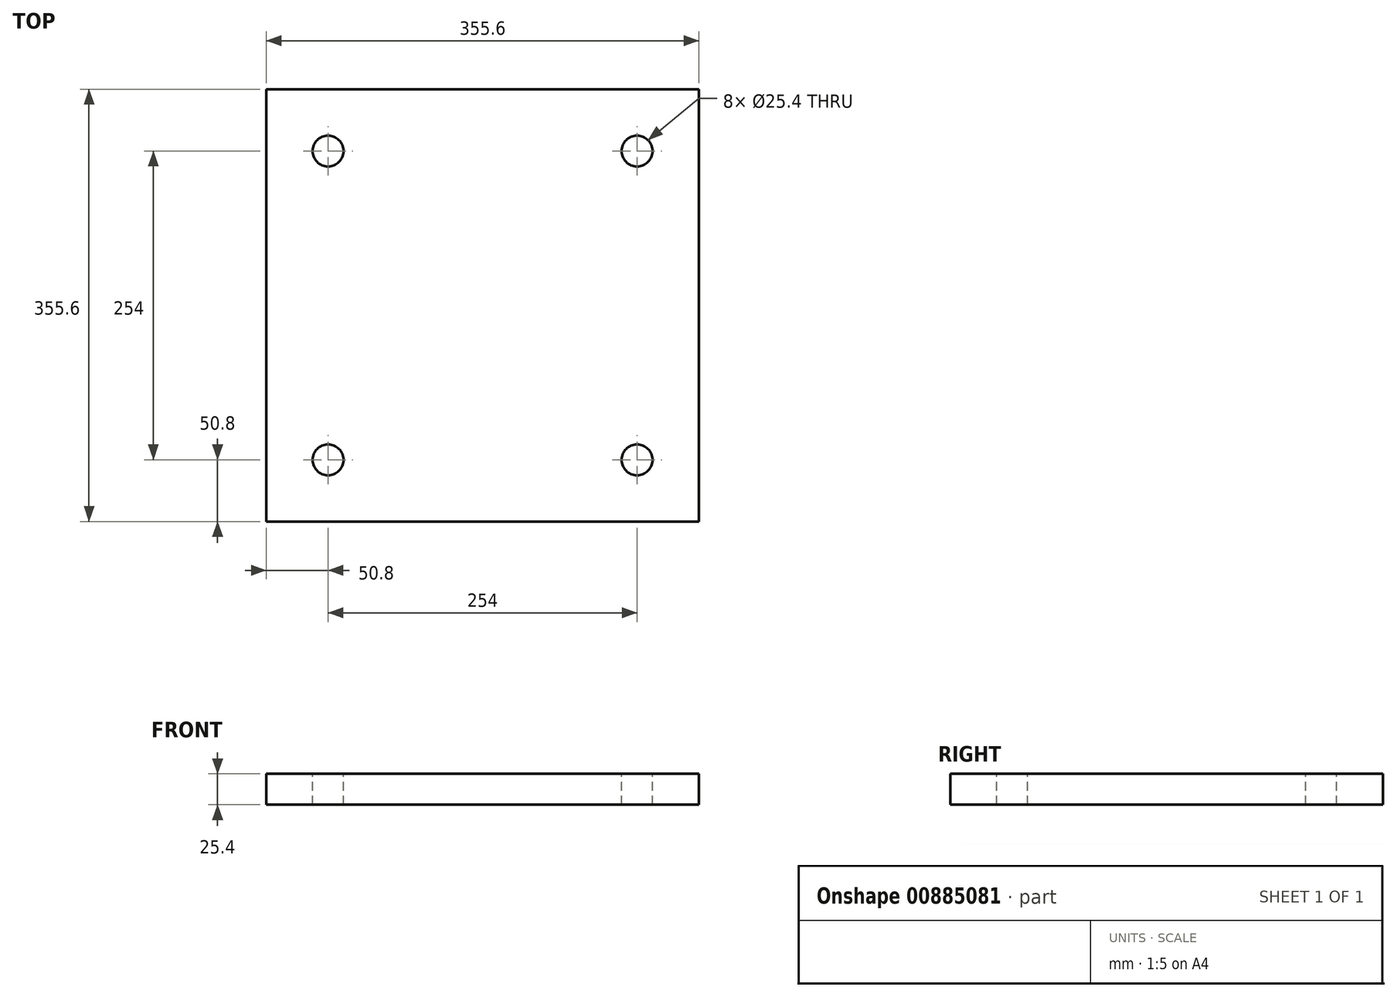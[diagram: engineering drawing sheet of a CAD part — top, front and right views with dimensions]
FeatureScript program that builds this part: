
annotation { "Feature Type Name" : "Feature", "Feature Type Description" : "" }
export const myFeature = defineFeature(function(context is Context, id is Id, definition is map)
    precondition{}
    {
        {
            var Q0;
            Q0=qCreatedBy(makeId("Top.planeOp"),FACE);
            var sketch = newSketch(context, id + "F0", { "sketchPlane" : qUnion([Q0])});
            skLineSegment(sketch, "E0.bottom", {"start": v(177.8, -177.8) * mm, "end": v(-177.8, -177.8) * mm});
            skLineSegment(sketch, "E0.top", {"start": v(177.8, 177.8) * mm, "end": v(-177.8, 177.8) * mm});
            skLineSegment(sketch, "E0.left", {"start": v(177.8, -177.8) * mm, "end": v(177.8, 177.8) * mm});
            skLineSegment(sketch, "E0.right", {"start": v(-177.8, -177.8) * mm, "end": v(-177.8, 177.8) * mm});
            skPoint(sketch, "E0.middle", {"position": v(0, 0) * mm});
            skSolve(sketch);
        }
        {
            var Q0;
            Q0=makeQuery(id+"F0.imprint","IMPRINT",FACE,{"disambiguationData":[TD([[makeQuery(id+"F0.imprint","IMPRINT",EDGE,{"derivedFrom":sQuery(id+"F0.wireOp",EDGE,"E0.bottom")}),-1.0]])]});
            extrude(context, id + "F1", {"entities" : qUnion([Q0]), "depth" : 25.4 * mm, "offsetDistance" : 25.4 * mm});
        }
        {
            var Q0;
            Q0=makeQuery(id+"F1.opExtrude","CAP_FACE",FACE,{"disambiguationData":[OSD([sQuery(id+"F0.wireOp",EDGE,"E0.bottom"),sQuery(id+"F0.wireOp",EDGE,"E0.top"),sQuery(id+"F0.wireOp",EDGE,"E0.left"),sQuery(id+"F0.wireOp",EDGE,"E0.right")])],"isStart":false});
            var sketch = newSketch(context, id + "F2", { "sketchPlane" : qUnion([Q0])});
            skPoint(sketch, "E1", {"position": v(22.28, -37.52) * mm});
            skPoint(sketch, "E2", {"position": v(0, 0) * mm});
            skSolve(sketch);
        }
        {
            var Q0;
            Q0=makeQuery(id+"F2.imprint","IMPRINT",FACE,{"disambiguationData":[TD([[makeQuery(id+"F2.imprint","IMPRINT",EDGE,{"derivedFrom":makeQuery(id+"F1.opExtrude","CAP_EDGE",EDGE,{"disambiguationData":[OSD([sQuery(id+"F0.wireOp",EDGE,"E0.bottom")])],"isStart":false})}),-1.0]])]});
            var sketch = newSketch(context, id + "F3", { "sketchPlane" : qUnion([Q0])});
            skLineSegment(sketch, "E3.bottom", {"start": v(-127, -127) * mm, "end": v(127, -127) * mm});
            skLineSegment(sketch, "E3.top", {"start": v(-127, 127) * mm, "end": v(127, 127) * mm});
            skLineSegment(sketch, "E3.left", {"start": v(-127, -127) * mm, "end": v(-127, 127) * mm});
            skLineSegment(sketch, "E3.right", {"start": v(127, -127) * mm, "end": v(127, 127) * mm});
            skPoint(sketch, "E3.middle", {"position": v(0, 0) * mm});
            skSolve(sketch);
        }
        {
            var Q0;
            Q0=sQuery(id+"F3.wireOp",VERTEX,"E3.bottom.start");
            var Q1;
            Q1=sQuery(id+"F3.wireOp",VERTEX,"E3.bottom.end");
            var Q2;
            Q2=sQuery(id+"F3.wireOp",VERTEX,"E3.top.end");
            var Q3;
            Q3=sQuery(id+"F3.wireOp",VERTEX,"E3.top.start");
            var Q4;
            Q4=makeQuery(id+"F1.opExtrude","SWEPT_BODY",BODY,{"disambiguationData":[OSD([sQuery(id+"F0.wireOp",EDGE,"E0.bottom"),sQuery(id+"F0.wireOp",EDGE,"E0.top"),sQuery(id+"F0.wireOp",EDGE,"E0.left"),sQuery(id+"F0.wireOp",EDGE,"E0.right")])]});
            hole(context, id + "F4", {"style" : HoleStyle.SIMPLE, "endStyle" : HoleEndStyle.THROUGH, "holeDiameter" : 25.4 * mm, "majorDiameter" : 6.35 * mm, "isTappedThrough" : true, "tappedDepth" : 12.7 * mm, "tapClearance" : 3, "locations" : qUnion([Q0, Q1, Q2, Q3]), "scope" : qUnion([Q4])});
        }
        {
            var Q0;
            Q0=makeQuery(id+"F2.imprint","IMPRINT",FACE,{"disambiguationData":[TD([[makeQuery(id+"F2.imprint","IMPRINT",EDGE,{"derivedFrom":makeQuery(id+"F1.opExtrude","CAP_EDGE",EDGE,{"disambiguationData":[OSD([sQuery(id+"F0.wireOp",EDGE,"E0.bottom")])],"isStart":false})}),-1.0]])]});
            var sketch = newSketch(context, id + "F5", { "sketchPlane" : qUnion([Q0])});
            skCircle(sketch, "E4", {"center": v(0, 0) * mm, "radius": 109.54 * mm});
            skCircle(sketch, "E5", {"center": v(0, 0) * mm, "radius": 101.36 * mm});
            skSolve(sketch);
        }
        {
            var Q0;
            Q0=sQuery(id+"F5.wireOp",EDGE,"E4");
            var Q1;
            Q1=sQuery(id+"F5.wireOp",EDGE,"E5");
            extrude(context, id + "F6", {"bodyType" : ToolBodyType.SURFACE, "surfaceEntities" : qUnion([Q0, Q1]), "depth" : 1574.8 * mm, "offsetDistance" : 25.4 * mm});
        }
    });
